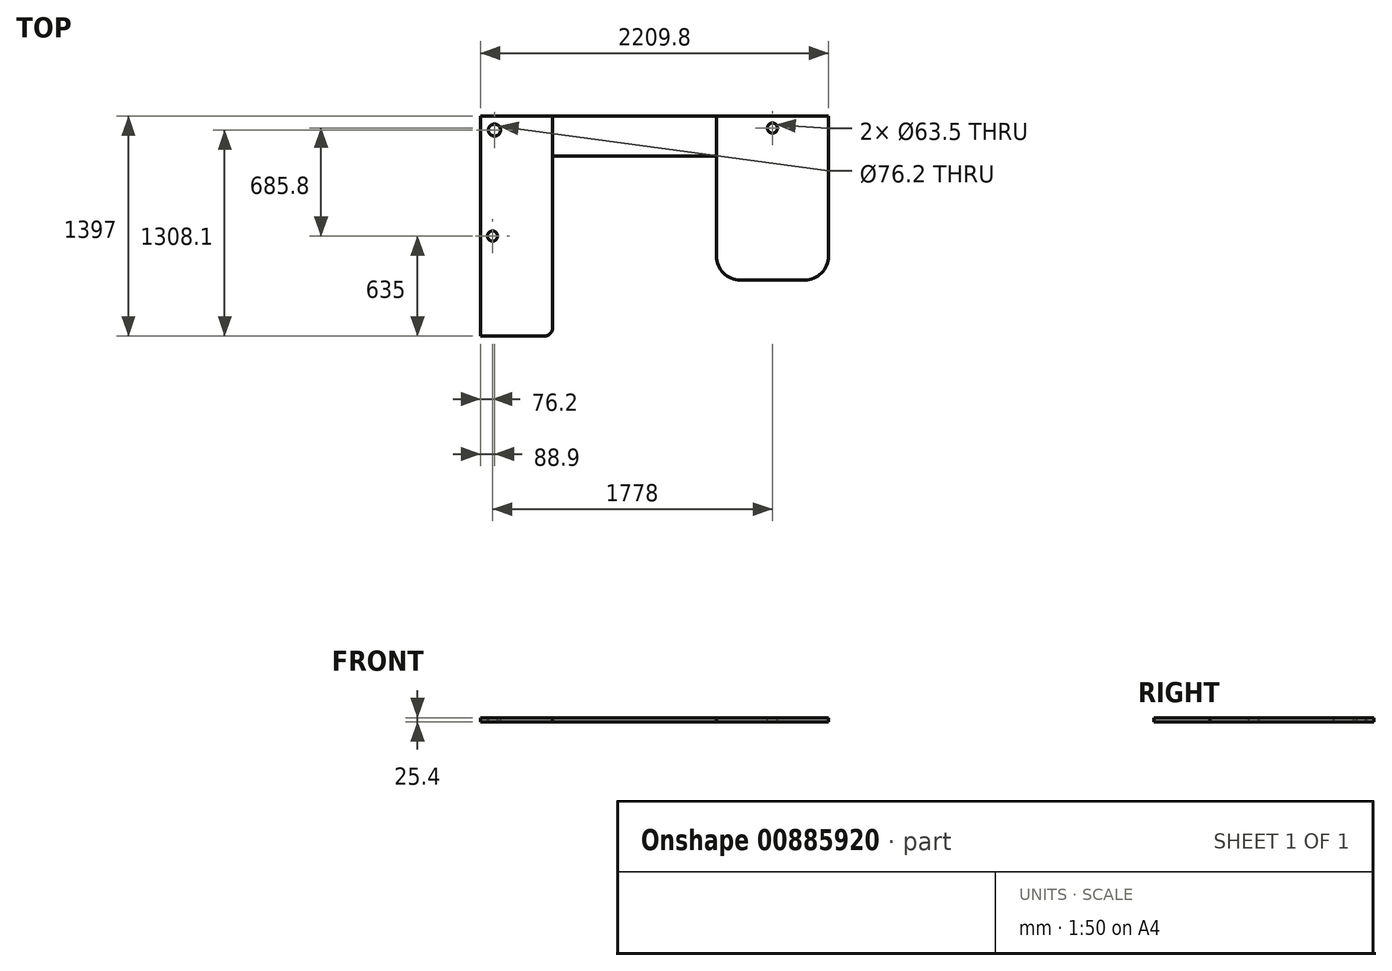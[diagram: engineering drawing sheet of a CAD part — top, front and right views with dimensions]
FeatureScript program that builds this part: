
annotation { "Feature Type Name" : "Feature", "Feature Type Description" : "" }
export const myFeature = defineFeature(function(context is Context, id is Id, definition is map)
    precondition{}
    {
        {
            var Q0;
            Q0=qCreatedBy(makeId("Top.planeOp"),FACE);
            var sketch = newSketch(context, id + "F0", { "sketchPlane" : qUnion([Q0])});
            skLineSegment(sketch, "E0.bottom", {"start": v(0, 0) * mm, "end": v(457.2, 0) * mm});
            skLineSegment(sketch, "E0.top", {"start": v(0, -1397) * mm, "end": v(457.2, -1397) * mm});
            skLineSegment(sketch, "E0.left", {"start": v(0, 0) * mm, "end": v(0, -1397) * mm});
            skLineSegment(sketch, "E0.right", {"start": v(457.2, 0) * mm, "end": v(457.2, -1397) * mm});
            skSolve(sketch);
        }
        {
            var Q0;
            Q0 = qSketchRegion(id + "F0", true);
            extrude(context, id + "F1", {"entities" : qUnion([Q0]), "oppositeDirection" : true, "depth" : 25.4 * mm, "offsetDistance" : 25.4 * mm});
        }
        {
            var Q0;
            Q0=qCreatedBy(makeId("Top.planeOp"),FACE);
            var sketch = newSketch(context, id + "F2", { "sketchPlane" : qUnion([Q0])});
            skLineSegment(sketch, "E1.bottom", {"start": v(457.2, 0) * mm, "end": v(1498.6, 0) * mm});
            skLineSegment(sketch, "E1.top", {"start": v(457.2, -254) * mm, "end": v(1498.6, -254) * mm});
            skLineSegment(sketch, "E1.left", {"start": v(457.2, 0) * mm, "end": v(457.2, -254) * mm});
            skLineSegment(sketch, "E1.right", {"start": v(1498.6, 0) * mm, "end": v(1498.6, -254) * mm});
            skSolve(sketch);
        }
        {
            var Q0;
            Q0 = qSketchRegion(id + "F2", true);
            extrude(context, id + "F3", {"entities" : qUnion([Q0]), "oppositeDirection" : true, "depth" : 25.4 * mm, "offsetDistance" : 25.4 * mm});
        }
        {
            var Q0;
            Q0=qCreatedBy(makeId("Top.planeOp"),FACE);
            var sketch = newSketch(context, id + "F4", { "sketchPlane" : qUnion([Q0])});
            skLineSegment(sketch, "E2.bottom", {"start": v(1498.6, 0) * mm, "end": v(2209.8, 0) * mm});
            skLineSegment(sketch, "E2.top", {"start": v(1498.6, -1041.4) * mm, "end": v(2209.8, -1041.4) * mm});
            skLineSegment(sketch, "E2.left", {"start": v(1498.6, 0) * mm, "end": v(1498.6, -1041.4) * mm});
            skLineSegment(sketch, "E2.right", {"start": v(2209.8, 0) * mm, "end": v(2209.8, -1041.4) * mm});
            skSolve(sketch);
        }
        {
            var Q0;
            Q0 = qSketchRegion(id + "F4", true);
            extrude(context, id + "F5", {"entities" : qUnion([Q0]), "oppositeDirection" : true, "depth" : 25.4 * mm, "offsetDistance" : 25.4 * mm});
        }
        {
            var Q0;
            Q0=makeQuery(id+"F1.opExtrude","SWEPT_EDGE",EDGE,{"disambiguationData":[OSD([sQuery(id+"F0.wireOp",EDGE,"E0.top"),sQuery(id+"F0.wireOp",EDGE,"E0.right")])]});
            fillet(context, id + "F6", {"entities" : qUnion([Q0]), "tangentPropagation" : true, "radius" : 50.8 * mm, "defaultsChanged" : true, "vertexSettings" : [], "allowEdgeOverflow" : false});
        }
        {
            var Q0;
            Q0=makeQuery(id+"F5.opExtrude","SWEPT_EDGE",EDGE,{"disambiguationData":[OSD([sQuery(id+"F4.wireOp",EDGE,"E2.top"),sQuery(id+"F4.wireOp",EDGE,"E2.right")])]});
            var Q1;
            Q1=makeQuery(id+"F5.opExtrude","SWEPT_EDGE",EDGE,{"disambiguationData":[OSD([sQuery(id+"F4.wireOp",EDGE,"E2.top"),sQuery(id+"F4.wireOp",EDGE,"E2.left")])]});
            fillet(context, id + "F7", {"entities" : qUnion([Q0, Q1]), "tangentPropagation" : true, "radius" : 152.4 * mm, "defaultsChanged" : true, "vertexSettings" : [], "allowEdgeOverflow" : false});
        }
        {
            var Q0;
            Q0=makeQuery(id+"F1.opExtrude","CAP_FACE",FACE,{"disambiguationData":[OSD([sQuery(id+"F0.wireOp",EDGE,"E0.bottom"),sQuery(id+"F0.wireOp",EDGE,"E0.top"),sQuery(id+"F0.wireOp",EDGE,"E0.left"),sQuery(id+"F0.wireOp",EDGE,"E0.right")])],"isStart":true});
            var sketch = newSketch(context, id + "F8", { "sketchPlane" : qUnion([Q0])});
            skCircle(sketch, "E3", {"center": v(88.9, -88.9) * mm, "radius": 38.1 * mm});
            skCircle(sketch, "E4", {"center": v(1854.2, -76.2) * mm, "radius": 31.75 * mm});
            skCircle(sketch, "E5", {"center": v(76.2, -762) * mm, "radius": 31.75 * mm});
            skLineSegment(sketch, "E6", {"start": v(1854.2, 0) * mm, "end": v(1854.2, -76.2) * mm, "construction": true});
            skSolve(sketch);
        }
        {
            var Q0;
            Q0 = qSketchRegion(id + "F8", true);
            extrude(context, id + "F9", {"entities" : qUnion([Q0]), "operationType" : NewBodyOperationType.REMOVE, "oppositeDirection" : true, "depth" : 25.4 * mm, "offsetDistance" : 25.4 * mm});
        }
    });
